# Revit family: Suszarka_do_rak_ORKAN 1900 W
name_source: partatom
category: Electrical Equipment
units: mm (PartAtom-declared; Revit-internal decimal feet)

## family parameters
Always vertical = Yes
Cut with Voids When Loaded = No
Host = Wall
Part Type = Panelboard
Room Calculation Point = No
Round Connector Dimension = Use Diameter
Shared = No

## types (1)
- DA1900SQB
    Color / Kolor = White / Biały
    Depth / Glebokosc = 210 mm  [stored 0.688976 ft]
    Description = Suszarka do rąk 1900W ORKAN to automatyczne urządzenie ze stali nierdzewnej  o matowym wykończeniu. Dzięki nowoczesnemu designowi idealnie pasuje do wymagań każdej modernistycznej toalety publicznej. Szybkość, wydajność i skuteczność tej elektrycznej suszarki do rąk sprawia, że jest ona polecana do miejsc o dużym nasileniu ruchu. Jest to suszarka kieszeniowa zawierająca 2 fotokomórki, którą charakteryzuje sposób suszenia rąk rozpoczynający się po umieszczeniu dłoni w przestrzeni zbliżonej wyglądem do kieszeni. Powietrze, wydostające się z dużą prędkością z wielu małych otworów wylotowych, suszy dłonie w sposób zapewniający użytkownikom najwyższy stopień higieny.
    Height / Wysokosc = 488 mm  [stored 1.60105 ft]
    Manufacturer = FANECO.com
    Manufacturer code / Kod producenta = 5901764296416
    Material finish / Wykonczenie = Stal nierdzewna, mat.
    Model = ORKAN
    Product code / Kod produktu = DA1900SQB
    Type Comments = Suszarka do rąk 1900 W ORKAN stal szlachetna matowa
    URL = https://faneco.com
    Wattage = 1900
    Weight / Waga = 9 kg
    Width / Szerokosc = 300 mm  [stored 0.984252 ft]

note: [stored X ft] marks values corroborated as IEEE doubles in the binary element streams (Revit-internal decimal feet)

## geometry (parser evidence)
native form markers: Sweep x17
no freeform markers — native parametric forms only
